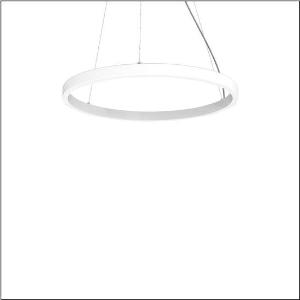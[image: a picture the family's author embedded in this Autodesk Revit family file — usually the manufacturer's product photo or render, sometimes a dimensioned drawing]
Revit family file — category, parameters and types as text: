
# Revit family: silica_r__21_ring-o_5pjbo3d1004a_d373
name_source: partatom
category: Lighting Fixtures
units: mm (PartAtom-declared; Revit-internal decimal feet)

## family parameters
Cut with Voids When Loaded = No
Host = Face
Light Source = No
Part Type = Normal
Room Calculation Point = No
Round Connector Dimension = Use Diameter
Shared = No

## types (1)
- Silica® 21 Ring-O (1 x LED, 6860 lm, 105 W, 3000K)
    Apparent Load = 105 VA
    CIE Flux Codes = 2 16 49 50 100
    Color Rendering = 80
    Color Temperature = 3000K
    Default Elevation = 1800 mm
    Description = Silica® 21 Ring-O, suspended luminaire, of PMMA, frosted, light emission: outer ring side luminous distribution, primary light characteristic: symmetric, installation type: suspended mounting, LED, rated luminous flux: 6.860lm, luminous efficacy: 65lm/W, light colour: 830, colour temperature: 3000K, with terminal, 5-pole, mains connection: 230V, AC/DC, 0/50..60Hz, rated input power: 105W, housing, of extruded aluminium section, traffic white (RAL 9016), diameter: 1.100mm, ceiling canopy, traffic white (RAL 9016), protection rating (lamp compartment): IP40, insulation class (complete): insulation class I (protective earthing), certification: CE, impact resistance: IK02, permissible operating ambient temperature: 0..+35°C, packaging unit: 1 piece
    Height = 48 mm  [stored 0.15748 ft]
    Lamp = 1 x LED
    Lamp Light Flux = 6860 lm
    Lamp Power = 105 W
    Lamp count = 1
    Length = 1100 mm
    Luminous efficacy = 65 lm/W
    Manufacturer = Siteco
    ModVariant = No
    Model = 5PJBO3D1004A
    Mounting Place = Ceiling
    Mounting Type = Pendant
    Number of Poles = 1
    OnlyDefault = Yes
    Power Factor = 1
    Product Name = Silica® 21 Ring-O
    Product group = suspended luminaire
    ProductGroupID = 904
    Protection Class = Protection class I
    Protection Degree = Degree of protection
    RLX_Detail_Level = 1
    RLX_Emergency_Light_Flux = 0 lm
    RLX_Emergency_Type = 0
    RLX_Emergency_Type_DB = No
    RlxData = <blob elided: 13521 chars, md5=d0384faa>
    Socket = socket
    Standby Power = 0 W
    System Light Flux = 6860 lm
    System Power = 105 W
    Type Comments = Product without accessories
    Type Image = l_1258387.jpg
    URL = http://relux.com
    VarID = ---
    Voltage = 0 V
    Weight = 0.00 kg
    Width = 0 mm  [stored 0 ft]

note: [stored X ft] marks values corroborated as IEEE doubles in the binary element streams (Revit-internal decimal feet)

## geometry (parser evidence)
native form markers: Sweep x13
no freeform markers — native parametric forms only
